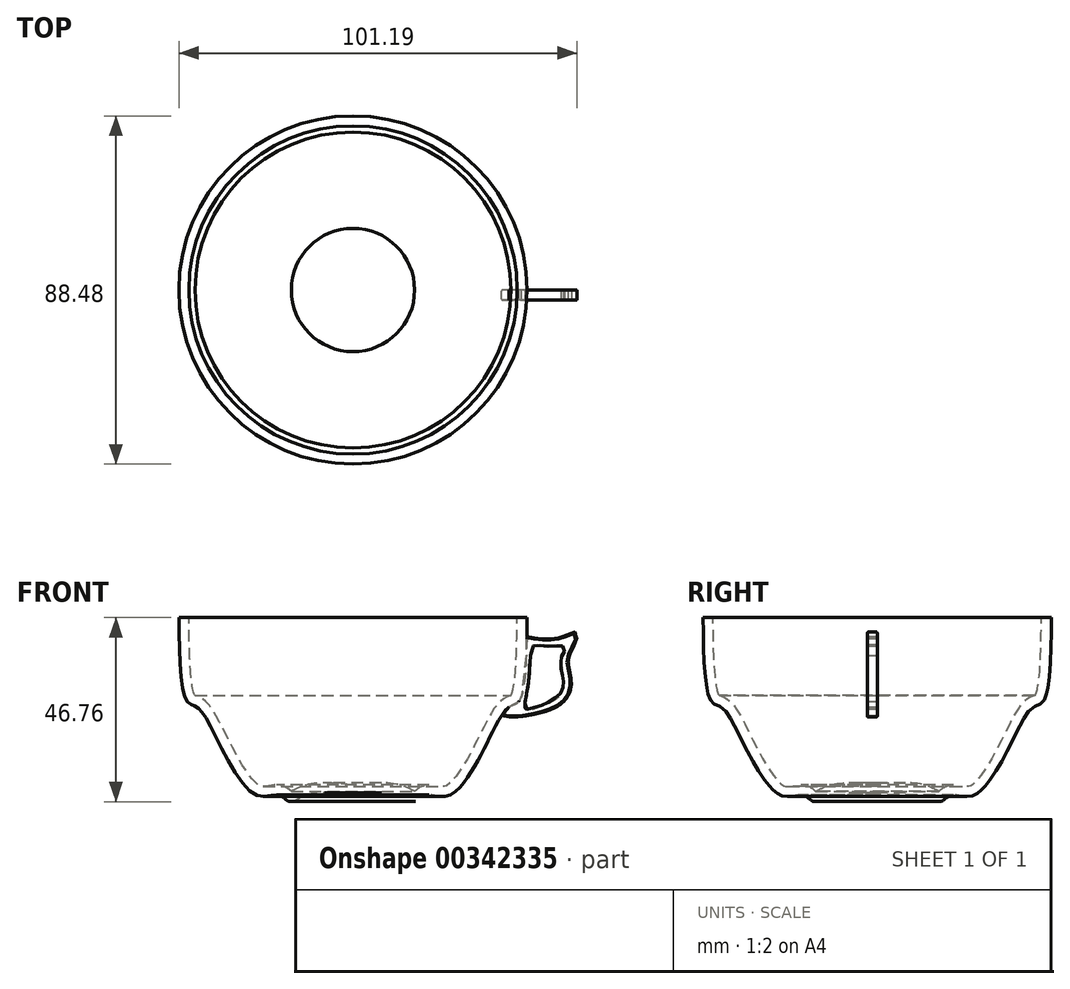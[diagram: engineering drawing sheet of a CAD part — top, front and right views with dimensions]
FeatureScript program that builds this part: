
annotation { "Feature Type Name" : "Feature", "Feature Type Description" : "" }
export const myFeature = defineFeature(function(context is Context, id is Id, definition is map)
    precondition{}
    {
        {
            var Q0;
            Q0=qCreatedBy(makeId("Front.planeOp"),FACE);
            var sketch = newSketch(context, id + "F0", { "sketchPlane" : qUnion([Q0])});
            skLineSegment(sketch, "E0", {"start": v(0, -26.13) * mm, "end": v(0, 68.42) * mm, "construction": true});
            skFitSpline(sketch, "E1", {"points": [v(0, 0) * mm, v(-11.65, 0) * mm, v(-16.17, -1.62) * mm, v(-18.8, 0) * mm, v(-24.65, 0) * mm, v(-36.14, 17.4) * mm, v(-39.9, 22.5) * mm, v(-42.17, 23.8) * mm, v(-44.24, 45.1) * mm], "startDerivative": vector(-87.3, 10) * mm, "endDerivative": vector(-1.84, 140.7) * mm});
            skLineSegment(sketch, "E2", {"start": v(-44.24, 45.1) * mm, "end": v(0, 45.1) * mm});
            skLineSegment(sketch, "E3", {"start": v(0, 45.1) * mm, "end": v(0, 0) * mm});
            skSolve(sketch);
        }
        {
            var Q0;
            Q0=makeQuery(id+"F0.imprint","IMPRINT",FACE,{"disambiguationData":[TD([[makeQuery(id+"F0.imprint","IMPRINT",EDGE,{"derivedFrom":sQuery(id+"F0.wireOp",EDGE,"E1")}),-1.0]])]});
            var Q1;
            Q1=sQuery(id+"F0.wireOp",EDGE,"E0");
            revolve(context, id + "F1", {"entities" : qUnion([Q0]), "axis" : qUnion([Q1]), "revolveType" : RevolveType.FULL});
        }
        {
            var Q0;
            Q0=qCreatedBy(makeId("Front.planeOp"),FACE);
            var sketch = newSketch(context, id + "F2", { "sketchPlane" : qUnion([Q0])});
            skFitSpline(sketch, "E4", {"points": [v(43.95, 40.31) * mm, v(52.58, 40) * mm, v(56.68, 41.36) * mm, v(56.57, 38.94) * mm, v(54.68, 34.63) * mm, v(55.42, 29.37) * mm, v(53.1, 23.37) * mm, v(41.53, 19.9) * mm, v(37.74, 20.22) * mm], "startDerivative": vector(57.34, -10.35) * mm, "endDerivative": vector(-29.33, 5.88) * mm});
            skLineSegment(sketch, "E5", {"start": v(43.95, 40.31) * mm, "end": v(43.95, 38.3) * mm});
            skLineSegment(sketch, "E6", {"start": v(43.95, 38.3) * mm, "end": v(43.95, 35.47) * mm});
            skLineSegment(sketch, "E7", {"start": v(43.95, 35.47) * mm, "end": v(42.79, 25.38) * mm});
            skLineSegment(sketch, "E8", {"start": v(42.79, 25.38) * mm, "end": v(42.2, 23.79) * mm});
            skLineSegment(sketch, "E9", {"start": v(42.2, 23.79) * mm, "end": v(39.6, 22.4) * mm});
            skLineSegment(sketch, "E10", {"start": v(39.6, 22.4) * mm, "end": v(37.74, 20.22) * mm});
            skSolve(sketch);
        }
        {
            var Q0;
            Q0=makeQuery(id+"F2.imprint","IMPRINT",FACE,{"disambiguationData":[TD([[makeQuery(id+"F2.imprint","IMPRINT",EDGE,{"derivedFrom":sQuery(id+"F2.wireOp",EDGE,"E4")}),-1.0]])]});
            extrude(context, id + "F3", {"entities" : qUnion([Q0]), "depth" : 2.54 * mm});
        }
        {
            var Q0;
            Q0=makeQuery(id+"F1.opRevolve","SWEPT_FACE",FACE,{"disambiguationData":[OSD([sQuery(id+"F0.wireOp",EDGE,"E2")])]});
            shell(context, id + "F4", {"entities" : qUnion([Q0]), "thickness" : 2.54 * mm});
        }
        {
            var Q0;
            Q0=makeQuery(id+"F3.opExtrude","CAP_FACE",FACE,{"disambiguationData":[OSD([sQuery(id+"F2.wireOp",EDGE,"E4"),sQuery(id+"F2.wireOp",EDGE,"E5"),sQuery(id+"F2.wireOp",EDGE,"E6"),sQuery(id+"F2.wireOp",EDGE,"E7"),sQuery(id+"F2.wireOp",EDGE,"E8"),sQuery(id+"F2.wireOp",EDGE,"E9"),sQuery(id+"F2.wireOp",EDGE,"E10")])],"isStart":false});
            var sketch = newSketch(context, id + "F5", { "sketchPlane" : qUnion([Q0])});
            skPoint(sketch, "E11.0.internal.snap0", {"position": v(43.95, 37.9) * mm});
            skPoint(sketch, "E11.1.internal.snap0", {"position": v(43.95, 37.9) * mm});
            skPoint(sketch, "E11.2.internal.snap0", {"position": v(43.95, 37.9) * mm});
            skPoint(sketch, "E11.3.internal.snap0", {"position": v(43.95, 37.9) * mm});
            skPoint(sketch, "E11.14.internal.snap0", {"position": v(43.95, 37.9) * mm});
            skPoint(sketch, "E11.15.internal.snap0", {"position": v(43.95, 37.9) * mm});
            skFitSpline(sketch, "E11", {"points": [v(45.83, 37.9) * mm, v(47.98, 37.9) * mm, v(51.2, 37.9) * mm, v(53.16, 37.9) * mm, v(53.72, 36.57) * mm, v(53, 35.2) * mm, v(52.81, 33.42) * mm, v(52.94, 31.83) * mm, v(53.36, 29.47) * mm, v(53.4, 28.15) * mm, v(52.96, 26.1) * mm, v(51.29, 24.64) * mm, v(48.64, 23.14) * mm, v(46.4, 22.37) * mm, v(43.95, 21.87) * mm, v(43.95, 25) * mm, v(44.77, 30.6) * mm, v(45.83, 37.9) * mm]});
            skSolve(sketch);
        }
        {
            var Q0;
            Q0=makeQuery(id+"F5.imprint","IMPRINT",FACE,{"disambiguationData":[TD([[makeQuery(id+"F5.imprint","IMPRINT",EDGE,{"derivedFrom":sQuery(id+"F5.wireOp",EDGE,"E11")}),-1.0]])]});
            extrude(context, id + "F6", {"entities" : qUnion([Q0]), "operationType" : NewBodyOperationType.REMOVE, "oppositeDirection" : true, "depth" : 25.4 * mm});
        }
        {
            var Q0;
            Q0=makeQuery(id+"F3.opExtrude","CAP_EDGE",EDGE,{"disambiguationData":[OSD([sQuery(id+"F2.wireOp",EDGE,"E4")])],"isStart":false});
            var Q1;
            Q1=makeQuery(id+"F3.opExtrude","CAP_EDGE",EDGE,{"disambiguationData":[OSD([sQuery(id+"F2.wireOp",EDGE,"E4")])],"isStart":true});
            var Q2;
            Q2=makeQuery(id+"F6.boolean.opBoolean","COPY",EDGE,{"derivedFrom":makeQuery(id+"F6.opExtrude","CAP_EDGE",EDGE,{"disambiguationData":[OSD([sQuery(id+"F5.wireOp",EDGE,"E11")])],"isStart":true})});
            var Q3;
            Q3=makeQuery(id+"F6.boolean.opBoolean","INTERSECT",EDGE,{"derivedFrom":[makeQuery(id+"F3.opExtrude","CAP_FACE",FACE,{"disambiguationData":[OSD([sQuery(id+"F2.wireOp",EDGE,"E4"),sQuery(id+"F2.wireOp",EDGE,"E5"),sQuery(id+"F2.wireOp",EDGE,"E6"),sQuery(id+"F2.wireOp",EDGE,"E7"),sQuery(id+"F2.wireOp",EDGE,"E8"),sQuery(id+"F2.wireOp",EDGE,"E9"),sQuery(id+"F2.wireOp",EDGE,"E10")])],"isStart":true}),makeQuery(id+"F6.opExtrude","SWEPT_FACE",FACE,{"disambiguationData":[OSD([sQuery(id+"F5.wireOp",EDGE,"E11")])]})]});
            fillet(context, id + "F7", {"entities" : qUnion([Q0, Q1, Q2, Q3]), "radius" : 0.25 * mm, "tangentPropagation" : true, "allowEdgeOverflow" : false});
        }
    });
